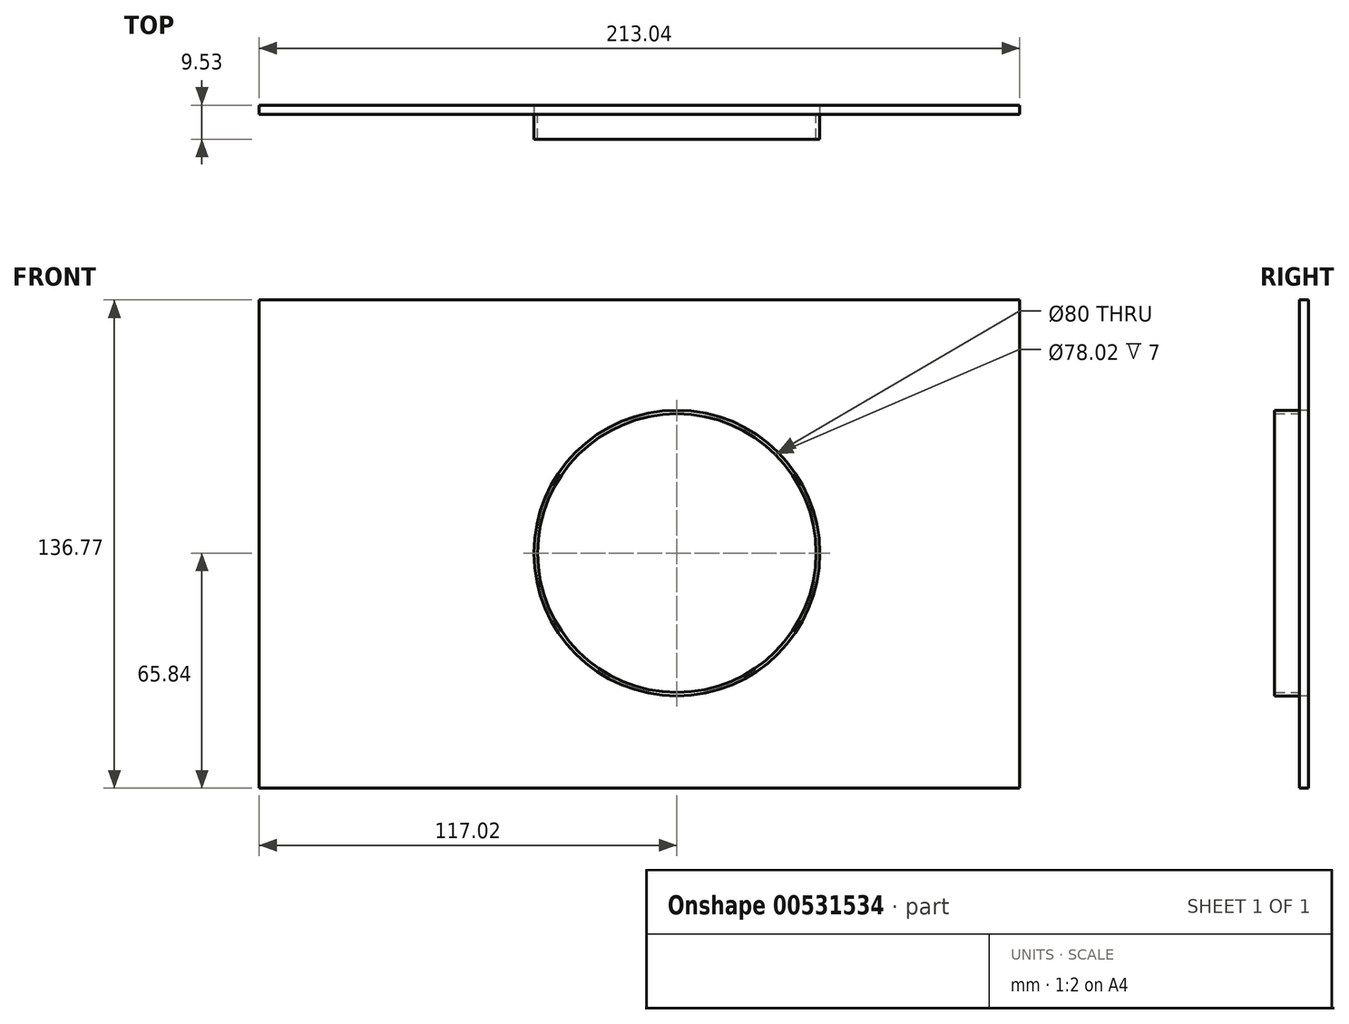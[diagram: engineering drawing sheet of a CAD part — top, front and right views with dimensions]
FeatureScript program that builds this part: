
annotation { "Feature Type Name" : "Feature", "Feature Type Description" : "" }
export const myFeature = defineFeature(function(context is Context, id is Id, definition is map)
    precondition{}
    {
        {
            var Q0;
            Q0=qCreatedBy(makeId("Front.planeOp"),FACE);
            var sketch = newSketch(context, id + "F0", { "sketchPlane" : qUnion([Q0])});
            skCircle(sketch, "E0", {"center": v(0, 0) * mm, "radius": 40 * mm});
            skCircle(sketch, "E1.0", {"center": v(0, 0) * mm, "radius": 39.01 * mm});
            skLineSegment(sketch, "E2.bottom", {"start": v(-92.02, 70.93) * mm, "end": v(96.02, 70.93) * mm});
            skLineSegment(sketch, "E2.top", {"start": v(-92.02, -65.84) * mm, "end": v(96.02, -65.84) * mm});
            skLineSegment(sketch, "E2.left", {"start": v(-92.02, 70.93) * mm, "end": v(-92.02, -65.84) * mm});
            skLineSegment(sketch, "E2.right", {"start": v(96.02, 70.93) * mm, "end": v(96.02, -65.84) * mm});
            skSolve(sketch);
        }
        {
            var Q0;
            Q0=makeQuery(id+"F0.imprint","IMPRINT",FACE,{"disambiguationData":[TD([[makeQuery(id+"F0.imprint","IMPRINT",EDGE,{"derivedFrom":sQuery(id+"F0.wireOp",EDGE,"E0")}),1.0]])]});
            extrude(context, id + "F1", {"entities" : qUnion([Q0]), "depth" : 7 * mm, "offsetDistance" : 25 * mm});
        }
        {
            var Q0;
            Q0=makeQuery(id+"F0.imprint","IMPRINT",FACE,{"disambiguationData":[TD([[makeQuery(id+"F0.imprint","IMPRINT",EDGE,{"derivedFrom":sQuery(id+"F0.wireOp",EDGE,"E0")}),-1.0]])]});
            extrude(context, id + "F2", {"entities" : qUnion([Q0]), "oppositeDirection" : true, "depth" : 0.93 * mm, "offsetDistance" : 25 * mm});
        }
        {
            var Q0;
            Q0=makeQuery(id+"F2.opExtrude","CAP_FACE",FACE,{"disambiguationData":[OSD([sQuery(id+"F0.wireOp",EDGE,"E0"),sQuery(id+"F0.wireOp",EDGE,"E2.bottom"),sQuery(id+"F0.wireOp",EDGE,"E2.top"),sQuery(id+"F0.wireOp",EDGE,"E2.left"),sQuery(id+"F0.wireOp",EDGE,"E2.right")])],"isStart":false});
            extrude(context, id + "F3", {"entities" : qUnion([Q0]), "operationType" : NewBodyOperationType.ADD, "depth" : 9.6 * mm, "offsetDistance" : 25 * mm});
        }
        {
            var Q0;
            {var subQ0=sQuery(id+"F0.wireOp",EDGE,"E2.left");Q0=makeQuery(id+"F3.boolean.opBoolean","MERGE",FACE,{"derivedFrom":[makeQuery(id+"F2.opExtrude","SWEPT_FACE",FACE,{"disambiguationData":[OSD([subQ0])]}),makeQuery(id+"F3.opExtrude","SWEPT_FACE",FACE,{"disambiguationData":[OSD([subQ0])]})]});}
            var Q1;
            {var subQ0=sQuery(id+"F0.wireOp",EDGE,"E2.right");Q1=makeQuery(id+"F3.boolean.opBoolean","MERGE",FACE,{"derivedFrom":[makeQuery(id+"F2.opExtrude","SWEPT_FACE",FACE,{"disambiguationData":[OSD([subQ0])]}),makeQuery(id+"F3.opExtrude","SWEPT_FACE",FACE,{"disambiguationData":[OSD([subQ0])]})]});}
            extrude(context, id + "F4", {"entities" : qUnion([Q0, Q1]), "operationType" : NewBodyOperationType.ADD, "depth" : 25 * mm, "offsetDistance" : 25 * mm});
        }
        {
            var Q0;
            {var subQ0=sQuery(id+"F0.wireOp",EDGE,"E2.left");Q0=makeQuery(id+"F4.boolean.opBoolean","MERGE",FACE,{"derivedFrom":[makeQuery(id+"F3.opExtrude","CAP_FACE",FACE,{"disambiguationData":[OSD([sQuery(id+"F0.wireOp",EDGE,"E0"),sQuery(id+"F0.wireOp",EDGE,"E2.bottom"),sQuery(id+"F0.wireOp",EDGE,"E2.top"),subQ0,sQuery(id+"F0.wireOp",EDGE,"E2.right")])],"isStart":false}),makeQuery(id+"F4.opExtrude","SWEPT_FACE",FACE,{"disambiguationData":[OSD([subQ0]),TDD([makeQuery(id+"F3.opExtrude","CAP_EDGE",EDGE,{"disambiguationData":[OSD([subQ0])],"isStart":false})])]})]});}
            extrude(context, id + "F5", {"entities" : qUnion([Q0]), "operationType" : NewBodyOperationType.REMOVE, "oppositeDirection" : true, "depth" : 8 * mm, "offsetDistance" : 25 * mm});
        }
    });
